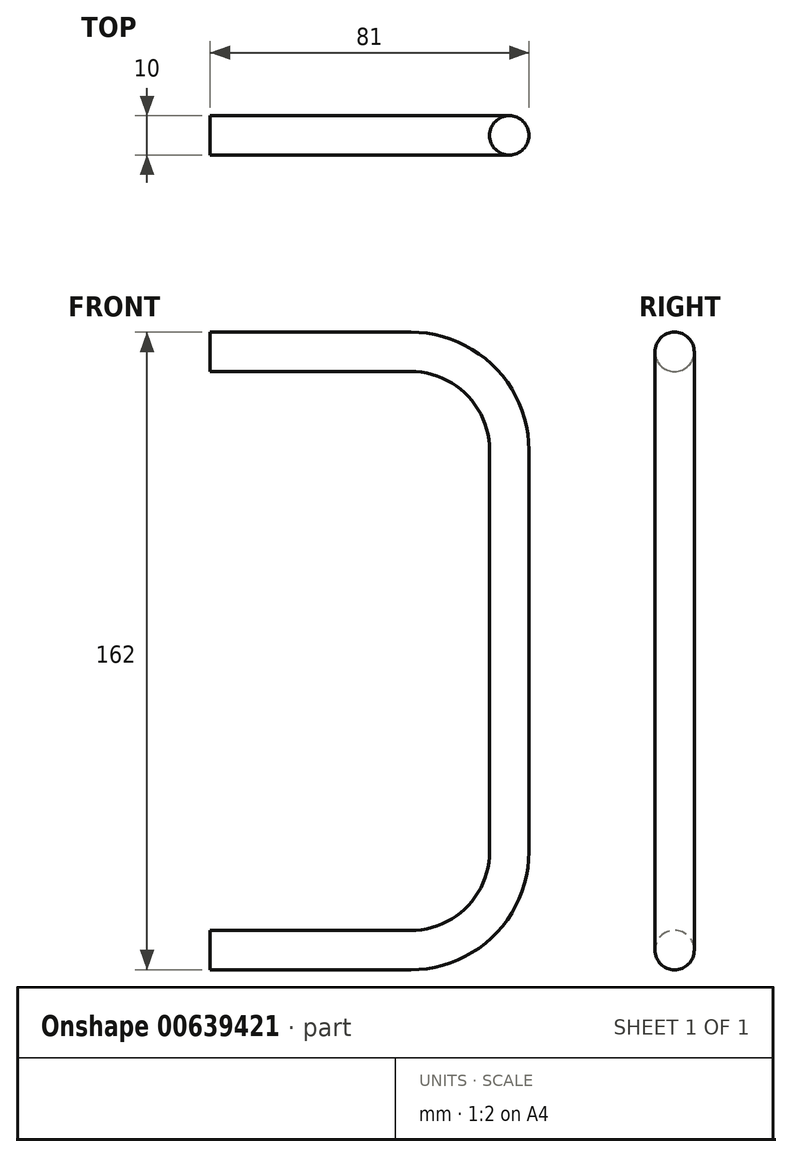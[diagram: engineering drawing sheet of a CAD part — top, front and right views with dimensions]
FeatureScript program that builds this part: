
annotation { "Feature Type Name" : "Feature", "Feature Type Description" : "" }
export const myFeature = defineFeature(function(context is Context, id is Id, definition is map)
    precondition{}
    {
        {
            var Q0;
            Q0=qCreatedBy(makeId("Front.planeOp"),FACE);
            var sketch = newSketch(context, id + "F0", { "sketchPlane" : qUnion([Q0])});
            skLineSegment(sketch, "E0", {"start": v(0, 0) * mm, "end": v(51, 0) * mm});
            skLineSegment(sketch, "E1", {"start": v(76, 25) * mm, "end": v(76, 127) * mm});
            skLineSegment(sketch, "E2", {"start": v(51, 152) * mm, "end": v(0, 152) * mm});
            skPoint(sketch, "E3.visualSharp", {"position": v(76, 152) * mm});
            skArc(sketch, "E3.filletArc", {"start": v(76, 127) * mm, "mid": v(68.68, 144.68) * mm, "end": v(51, 152) * mm});
            skPoint(sketch, "E4.visualSharp", {"position": v(76, 0) * mm});
            skArc(sketch, "E4.filletArc", {"start": v(51, 0) * mm, "mid": v(68.68, 7.32) * mm, "end": v(76, 25) * mm});
            skSolve(sketch);
        }
        {
            var Q0;
            Q0=qCreatedBy(makeId("Right.planeOp"),FACE);
            var sketch = newSketch(context, id + "F1", { "sketchPlane" : qUnion([Q0])});
            skCircle(sketch, "E5", {"center": v(0, 0) * mm, "radius": 5 * mm});
            skSolve(sketch);
        }
        {
            var Q0;
            Q0=makeQuery(id+"F1.imprint","IMPRINT",FACE,{"disambiguationData":[TD([[makeQuery(id+"F1.imprint","IMPRINT",EDGE,{"derivedFrom":sQuery(id+"F1.wireOp",EDGE,"E5")}),1.0]])]});
            var Q1;
            Q1=sQuery(id+"F0.wireOp",EDGE,"E2");
            var Q2;
            Q2=sQuery(id+"F0.wireOp",EDGE,"E3.filletArc");
            var Q3;
            Q3=sQuery(id+"F0.wireOp",EDGE,"E1");
            var Q4;
            Q4=sQuery(id+"F0.wireOp",EDGE,"E4.filletArc");
            var Q5;
            Q5=sQuery(id+"F0.wireOp",EDGE,"E0");
            sweep(context, id + "F2", {"profiles" : qUnion([Q0]), "path" : qUnion([Q1, Q2, Q3, Q4, Q5])});
        }
    });
